# Revit family: 14898 Беседка «Листопад» Хоббика
name_source: partatom
category: Антураж
revit_build: Autodesk Revit 2018 (Build: 20180423_1000(x64)
units: mm (PartAtom-declared; Revit-internal decimal feet)

## family parameters
Всегда вертикально = Да
Источник визуального образа = Геометрия семейства
На основе рабочей плоскости = Нет
Общий = Нет
При загрузке вырезать с полостями = Нет
Точка расчета площади = Нет

## types (3) — shared parameters
URL = https://hobbyka.ru
Артикул товара = Арт. 14898
Высота = 2400 мм
Группа модели = Навесы и беседки
Длина = 2380 мм
Изготовитель = ООО «Хоббика»
Материал изделия = Сталь, дерево
Цвет каркаса = Сталь
Цвет отделки = Дерево
Ширина = 2400 мм

## per-type parameters (varying)
| type | Изображение типоразмера | Описание | Стол | Шахматный стол и полки |
| Версия "Стандарт" | Беседка «Листопад» со столом Арт 14898.jpg | Беседка «Листопад». Версия стандарт | Нет | Нет |
| Версия "Со столом" | Беседка «Листопад» со столом Арт 14898.jpg | Беседка «Листопад». Версия со столом | Да | Нет |
| Версия "С шахматным столом и полками" | Беседка «Листопад» с шахматным столом и полками Арт 14898.jpg | Беседка «Листопад». Версия со столом | Да | Да |
